# Revit family: РИДАН_Компенсатор под приварку без кожуха
name_source: partatom
category: Арматура трубопроводов
units: mm (PartAtom-declared; Revit-internal decimal feet)

## family parameters
Всегда вертикально = Да
На основе рабочей плоскости = Нет
Общий = Нет
При загрузке вырезать с полостями = Нет
Размер круглого соединителя = Использовать диаметр
Тип детали = Вставляется

## types (14) — shared parameters
ADSK_Версия Revit = 2019
ADSK_Версия семейства = 1.0
ADSK_Единица измерения = шт.
ADSK_Завод-изготовитель = ООО «Ридан-Трейд»
ADSK_Количество = 1
ADSK_Марка = Компенсатор
ADSK_Расход жидкости = 0 м³/ч
LT = Table
URL = https://ridan.ru
Изготовитель = ООО «Ридан-Трейд»

## per-type parameters (varying)
| type | ADSK_Диаметр условный | ADSK_Код изделия | ADSK_Масса | ADSK_Наименование | a | a1 | b | b2 | c | d | e | num |
| DN 15 | 15 мм | 065H0040R | 0.75 | Компенсатор PN16 DN15, перемещение: +12/-28mm, внутренняя гильза, под приварку | 280 мм | 280 мм | 20 мм | 20 мм | 35 мм | 155 мм | 170 мм | 2 |
| DN 20 | 20 мм | 065H0041R | 0.77 | Компенсатор PN16 DN20, перемещение: +12/-28mm, внутренняя гильза, под приварку | 280 мм | 280 мм | 26 мм | 26 мм | 35 мм | 155 мм | 164 мм | 2 |
| DN 25 | 25 мм | 065H0042R | 1.11 | Компенсатор PN16 DN25, перемещение +12/-28mm, внутренняя гильза, под приварку | 275 мм | 275 мм | 32 мм | 32 мм | 44 мм | 150 мм | 162 мм | 2 |
| DN 32 | 32 мм | 065H0043R | 1.6 | Компенсатор PN16 DN32, перемещение: +12/-28mm, внутренняя гильза, под приварку | 310 мм | 310 мм | 42 мм | 42 мм | 51 мм | 163 мм | 172 мм | 2 |
| DN 40 | 40 мм | 065H0044R | 2.45 | Компенсатор PN16 DN40, перемещение: +12/-28mm, внутренняя гильза, под приварку | 310 мм | 310 мм | 45 мм | 45 мм | 65 мм | 163 мм | 183 мм | 2 |
| DN 50 | 50 мм | 065H0045R | 2.3 | Компенсатор PN16 DN50, перемещение: +12/-28mm, внутренняя гильза, под приварку | 310 мм | 310 мм | 57 мм | 57 мм | 65 мм | 163 мм | 171 мм | 2 |
| DN 65 | 65 мм | 065H0046R | 1.2 | Компенсатор PN16 DN65, перемещение: +12/-28mm, внутренняя гильза, под приварку | 250 мм | 250 мм | 76 мм | 76 мм | 96 мм | 129 мм | 149 мм | 2 |
| DN 80 | 80 мм | 065H0047R | 1.59 | Компенсатор PN16 DN80, перемещение: +12/-28mm, внутренняя гильза, под приварку | 255 мм | 255 мм | 89 мм | 89 мм | 111 мм | 132 мм | 154 мм | 2 |
| DN 100 | 100 мм | 065H0048R | 5.53 | Компенсатор PN16 DN100, перемещение +12/-28mm, внутренняя гильза, под приварку | 255 мм | 255 мм | 108 мм | 108 мм | 137 мм | 136 мм | 165 мм | 2 |
| DN 125 | 125 мм | 082X9242R | 3.5 | Осевой сильфонный компенсатор для СО Ду125/Ру16 +12/-28мм с внутр. направляющей, под приварку | 255 мм | 255 мм | 133 мм | 133 мм | 160 мм | 132 мм | 159 мм | 2 |
| DN 150 | 150 мм | 082X9243R | 5 | Осевой сильфонный компенсатор для СО Ду150/Ру16 +12/-28мм с внутр. направляющей, под приварку | 270 мм | 270 мм | 159 мм | 159 мм | 190 мм | 144 мм | 175 мм | 2 |
| DN 200 | 200 мм | 082X9244R | 8.5 | Осевой сильфонный компенсатор для СО Ду200/Ру16 +12/-28мм с внутр. направляющей, под приварку | 260 мм | 260 мм | 219 мм | 219 мм | 255 мм | 126 мм | 162 мм | 2 |
| DN 250 | 250 мм | 082X9245R | 13 | Осевой сильфонный компенсатор для СО Ду250/Ру16 +12/-28мм с внутр. направляющей, под приварку | 280 мм | 280 мм | 273 мм | 273 мм | 316 мм | 141 мм | 184 мм | 2 |
| DN 300 | 300 мм | 082X9246R | 17.5 | Осевой сильфонный компенсатор для СО Ду300/Ру16 +12/-28мм с внутр. направляющей, под приварку | 270 мм | 266 мм | 324 мм | 305 мм | 370 мм | 127 мм | 173 мм | 1 |
